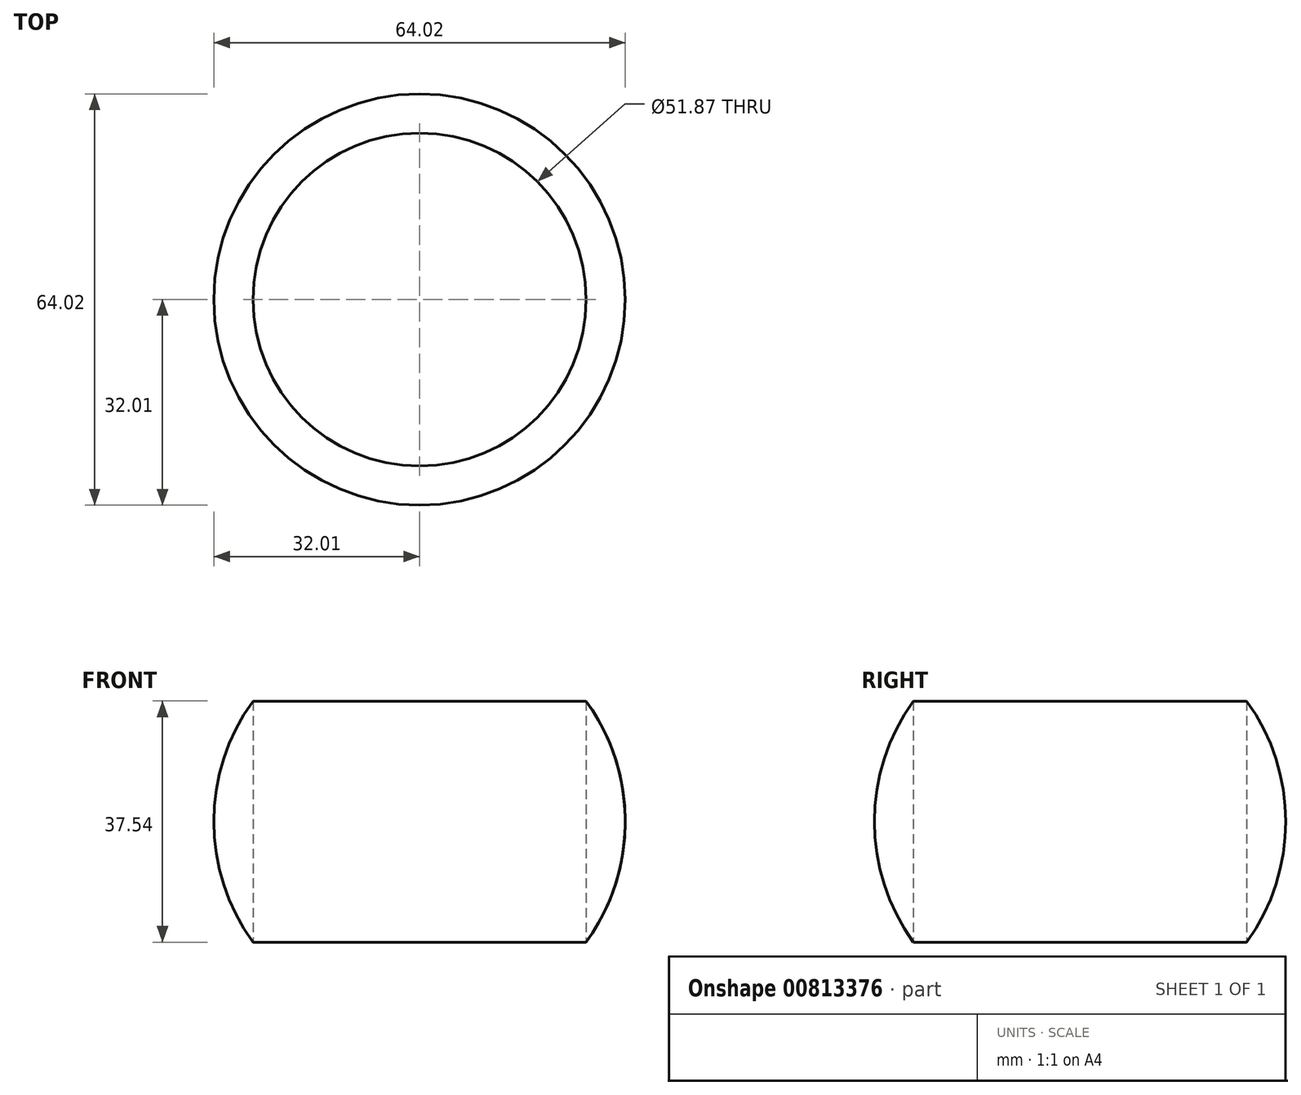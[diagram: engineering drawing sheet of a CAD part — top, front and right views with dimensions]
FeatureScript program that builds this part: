
annotation { "Feature Type Name" : "Feature", "Feature Type Description" : "" }
export const myFeature = defineFeature(function(context is Context, id is Id, definition is map)
    precondition{}
    {
        {
            var Q0;
            Q0=qCreatedBy(makeId("Top.planeOp"),FACE);
            var sketch = newSketch(context, id + "F0", { "sketchPlane" : qUnion([Q0])});
            skCircle(sketch, "E0", {"center": v(0, 0) * mm, "radius": 28.07 * mm});
            skSolve(sketch);
        }
        {
            var Q0;
            Q0=qCreatedBy(makeId("Front.planeOp"),FACE);
            var sketch = newSketch(context, id + "F1", { "sketchPlane" : qUnion([Q0])});
            skArc(sketch, "E1", {"start": v(0, 32.01) * mm, "mid": v(-32.01, 0) * mm, "end": v(0, -32.01) * mm});
            skLineSegment(sketch, "E2", {"start": v(0, 32.01) * mm, "end": v(0, -32.01) * mm});
            skSolve(sketch);
        }
        {
            var Q0;
            Q0=makeQuery(id+"F1.imprint","IMPRINT",FACE,{"disambiguationData":[TD([[makeQuery(id+"F1.imprint","IMPRINT",EDGE,{"derivedFrom":sQuery(id+"F1.wireOp",EDGE,"E1")}),1.0]])]});
            var Q1;
            Q1=sQuery(id+"F1.wireOp",EDGE,"E2");
            revolve(context, id + "F2", {"surfaceOperationType" : NewSurfaceOperationType.NEW, "entities" : qUnion([Q0]), "axis" : qUnion([Q1]), "revolveType" : RevolveType.FULL});
        }
        {
            var Q0;
            Q0=sQuery(id+"F0.wireOp",EDGE,"E0");
            extrude(context, id + "F3", {"bodyType" : ToolBodyType.SURFACE, "operationType" : NewBodyOperationType.REMOVE, "surfaceEntities" : qUnion([Q0]), "oppositeDirection" : true, "depth" : 57.1 * mm, "offsetDistance" : 25 * mm});
        }
        {
            var Q0;
            Q0=qCreatedBy(makeId("Top.planeOp"),FACE);
            cPlane(context, id + "F4", {"entities" : qUnion([Q0]), "cplaneType" : CPlaneType.OFFSET, "offset" : 56.8 * mm, "oppositeDirection" : true, "width" : 150 * mm, "height" : 150 * mm});
        }
        {
            var Q0;
            Q0=qCreatedBy(id+"F4.planeOp",FACE);
            var sketch = newSketch(context, id + "F5", { "sketchPlane" : qUnion([Q0])});
            skCircle(sketch, "E3", {"center": v(0, 0) * mm, "radius": 25.93 * mm});
            skSolve(sketch);
        }
        {
            var Q0;
            Q0=makeQuery(id+"F5.imprint","IMPRINT",FACE,{"disambiguationData":[TD([[makeQuery(id+"F5.imprint","IMPRINT",EDGE,{"derivedFrom":sQuery(id+"F5.wireOp",EDGE,"E3")}),1.0]])]});
            extrude(context, id + "F6", {"entities" : qUnion([Q0]), "operationType" : NewBodyOperationType.REMOVE, "depth" : 176.9 * mm, "offsetDistance" : 25 * mm});
        }
    });
